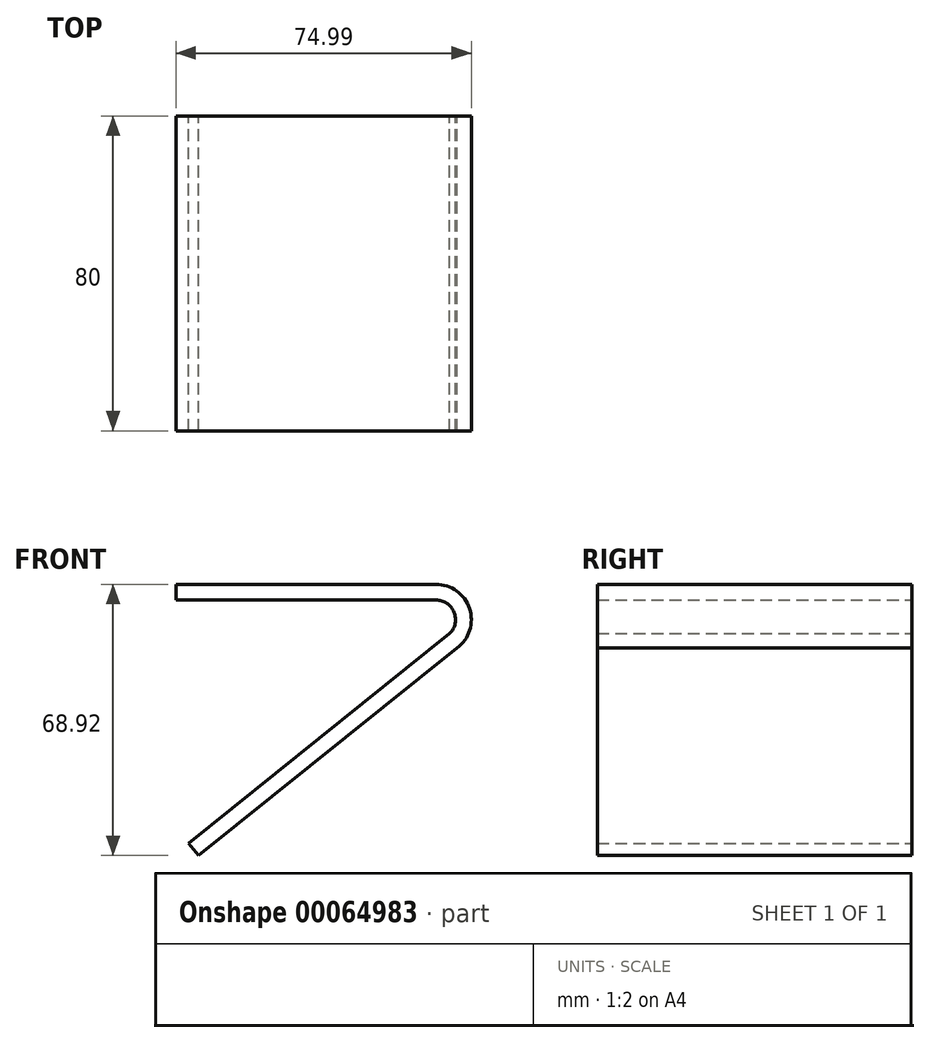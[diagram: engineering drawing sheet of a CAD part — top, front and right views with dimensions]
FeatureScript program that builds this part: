
annotation { "Feature Type Name" : "Feature", "Feature Type Description" : "" }
export const myFeature = defineFeature(function(context is Context, id is Id, definition is map)
    precondition{}
    {
        {
            var Q0;
            Q0=qCreatedBy(makeId("Front.planeOp"),FACE);
            var sketch = newSketch(context, id + "F0", { "sketchPlane" : qUnion([Q0])});
            skArc(sketch, "E0", {"start": v(5.37, -7.22) * mm, "mid": v(8.54, 2.83) * mm, "end": v(0, 9) * mm});
            skArc(sketch, "E1", {"start": v(3.53, -3.54) * mm, "mid": v(4.62, 1.9) * mm, "end": v(0, 5) * mm});
            skLineSegment(sketch, "E2", {"start": v(0, 5) * mm, "end": v(-65.99, 5) * mm});
            skLineSegment(sketch, "E3", {"start": v(-65.99, 5) * mm, "end": v(-65.99, 9) * mm});
            skLineSegment(sketch, "E4", {"start": v(-65.99, 9) * mm, "end": v(0, 9) * mm});
            skLineSegment(sketch, "E5", {"start": v(3.53, -3.54) * mm, "end": v(-62.85, -56.8) * mm});
            skLineSegment(sketch, "E6", {"start": v(-62.85, -56.8) * mm, "end": v(-60.34, -59.92) * mm});
            skLineSegment(sketch, "E7", {"start": v(-60.34, -59.92) * mm, "end": v(5.37, -7.22) * mm});
            skSolve(sketch);
        }
        {
            var Q0;
            Q0=makeQuery(id+"F0.imprint","IMPRINT",FACE,{"disambiguationData":[TD([[makeQuery(id+"F0.imprint","IMPRINT",EDGE,{"derivedFrom":sQuery(id+"F0.wireOp",EDGE,"E0")}),1.0]])]});
            extrude(context, id + "F1", {"entities" : qUnion([Q0]), "depth" : 80 * mm});
        }
    });
